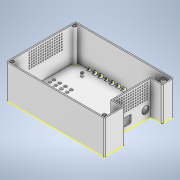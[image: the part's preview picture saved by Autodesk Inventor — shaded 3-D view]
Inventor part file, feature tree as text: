
AUTODESK INVENTOR PART (.ipt)
format: ipt  version: 2022 (Build 260153000, 153)  size: 842,752 bytes
history: native  units: mm
features: sketch x24, extrude x14, fillet x8, thread x7, hole x4, pattern_linear x3, shell x1, projected_geometry x1
ambient origin geometry x8: Origin, YZ Plane, XZ Plane, XY Plane, X Axis, Y Axis, Z Axis, Center Point
bodies: Solid1 (feature_tree)
feature tree (62):
  extrude  "Extrusion1"  Depth=120.0mm
  shell  "Shell1"  Thickness=35.0mm
  sketch  "Sketch2"  dims[d3=20.0mm d4=20.0mm]
  extrude  "Extrusion2"  Depth=20.0mm
  extrude  "Extrusion3"  Depth=2.0mm
  extrude  "Extrusion4"  Depth=6.0mm
  fillet  "Fillet1"  Radius=6.0mm
  fillet  "Fillet2"  Radius=6.0mm
  extrude  "Extrusion5"  Depth=80.0mm TaperAngle=0.0deg
  fillet  "Fillet3"  Radius=7.5mm
  fillet  "Fillet4"  Radius=13.0mm
  fillet  "Fillet5"  Radius=16.0mm
  extrude  "Extrusion6"  Depth=53.0mm
  hole  "Hole1"  [1 undecoded]
  pattern_linear  "Rectangular Pattern1"  Count1=8 Spacing1=0.0mm
  sketch  "Sketch9"  dims[d26=2.0mm d27=2.0mm d31=80.0mm d32=0.0mm]
  extrude  "Extrusion7"  Depth=2.0mm
  pattern_linear  "Rectangular Pattern2"  Count1=8 Spacing1=0.0mm
  extrude  "Extrusion8"  Depth=0.2mm
  pattern_linear  "Rectangular Pattern3"  Count1=2  [1 undecoded]
  fillet  "Fillet6"  [1 undecoded]
  fillet  "Fillet7"  Radius=6.0mm
  fillet  "Fillet8"  Radius=150.0mm
  sketch  "Sketch12"  dims[d40=2.0mm d41=6.0mm d42=4.0mm d43=2.0mm d44=90.0deg d45=8.0mm d46=20.594885mm d47=150.0mm d49=4.0mm]
  sketch  "Sketch13"  dims[d50=70.0mm d52=4.0mm d53=5.0mm]
  extrude  "Extrusion9"  Depth=5.0mm
  extrude  "Extrusion10"  Depth=10.0mm
  sketch  "Sketch15"  dims[d59=40.0mm d61=10.0mm d62=5.0mm d63=0.0mm]
  sketch  "Sketch16"  dims[d64=100.0mm d66=10.0mm d67=1.0mm]
  hole  "Hole2"  [1 undecoded]
  hole  "Hole3"  [1 undecoded]
  extrude  "Extrusion11"  Depth=1.0mm
  extrude  "Extrusion12"  Depth=6.2mm
  extrude  "Extrusion13"  Depth=6.2mm
  extrude  "Extrusion14"  Depth=69.0mm
  hole  "Hole4"  [1 undecoded]
  thread  "Thread1"  [1 undecoded]
  thread  "Thread2"  [1 undecoded]
  thread  "Thread3"  [1 undecoded]
  sketch  "Sketch22"  dims[d86=5.0mm d87=3.708mm d88=3.023mm d89=2.0mm d90=14.3117mm d91=58.0mm d92=20.594885mm]
  sketch  "Sketch23"  dims[d93=5.0mm d94=6.0mm d95=4.0mm d96=2.0mm d97=90.0deg d98=58.0mm d99=20.594885mm d102=2.0mm]
  thread  "Thread4"  [1 undecoded]
  thread  "Thread5"  [1 undecoded]
  thread  "Thread6"  [1 undecoded]
  thread  "Thread7"  [1 undecoded]
  sketch  "Sketch24"  dims[d103=2.0mm d104=4.0mm d105=4.0mm d106=2.0mm d109=2.0mm d110=4.0mm d111=4.000234mm d112=2.0mm d113=5.0mm d114=0.0mm d115=0.0mm d116=0.0mm d117=10.0mm d118=0.0mm d119=5.0mm d120=5.0mm d121=5.0mm d122=5.0mm d123=0.0mm d124=3.0mm d125=6.0mm d126=4.0mm d127=2.0mm d128=90.0deg d129=4.5mm d130=0.0mm d131=4.5mm d132=0.0mm d133=4.5mm d134=0.0mm d135=4.5mm d136=0.0mm d137=58.0mm d138=0.0mm d139=58.0mm d140=0.0mm d141=58.0mm d142=0.0mm d143=58.0mm d144=0.0mm d65=0.872665mm]
  sketch  "Sketch1"  dims[d0=170.0mm d1=120.0mm d2=35.0mm]
  sketch  "Sketch3"  dims[d5=80.0mm d6=0.0mm d7=2.0mm]
  sketch  "Sketch4"  dims[d8=26.0mm d9=70.0mm d10=6.0mm d11=6.0mm]
  sketch  "Sketch5"  dims[d12=22.0mm d13=80.0mm d14=0.0mm d15=7.5mm d16=13.0mm d17=16.0mm]
  sketch  "Sketch6"  dims[d18=80.0mm d19=0.0mm d20=53.0mm]
  sketch  "Sketch7"  dims[d21=10.0mm d22=13.0mm]
  sketch  "Sketch8"  dims[d23=13.0mm d24=80.0mm d25=0.0mm]
  sketch  "Sketch10"  dims[d33=0.2mm d34=0.2mm]
  sketch  "Sketch11"  dims[d35=2.0mm d36=20.0mm d37=0.0mm d38=0.0mm d39=6.0mm]
  sketch  "Sketch14"  dims[d54=10.0mm d55=0.0mm d56=100.0mm d58=7.0mm]
  projected_geometry  "Projected Loop1"
  sketch  "Sketch17"  dims[d68=1.0mm d69=1.0mm]
  sketch  "Sketch18"  dims[d70=3.1mm d71=6.2mm]
  sketch  "Sketch19"  dims[d72=3.1mm d73=6.2mm]
  sketch  "Sketch20"  dims[d74=3.1mm d75=69.0mm]
  sketch  "Sketch21"  dims[d76=34.5mm d77=6.2mm d78=6.2mm d79=6.2mm d80=58.0mm d81=0.0mm d82=3.5mm d83=6.2mm d84=58.0mm d85=0.0mm]
note: 13 required parameter values undecoded (feature->parameter linkage not recoverable at this tier; creation-order binding heuristic only, values carry confidence <= 0.55)
